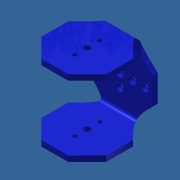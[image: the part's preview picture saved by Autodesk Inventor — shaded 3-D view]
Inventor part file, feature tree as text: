
AUTODESK INVENTOR PART (.ipt)
format: ipt  version: 2014 (Build 180170000, 170)  size: 280,576 bytes
history: native  units: in
note: dims shown in document units (in); Inventor stores cm internally (conversion verified against a paired STEP export)
features: extrude x7, sketch x7, plane x2, fillet x2, mirror x2, projected_geometry x2
ambient origin geometry x8: Origin, YZ Plane, XZ Plane, XY Plane, X Axis, Y Axis, Z Axis, Center Point
bodies: Solid1 (feature_tree)
feature tree (22):
  extrude  "Extrusion1"  TaperAngle=0.0deg  [1 undecoded]
  extrude  "Extrusion2"  Depth=0.1772in
  plane  "Work Plane1"
  extrude  "Extrusion3"  Depth=0.1772in
  fillet  "Fillet1"  [1 undecoded]
  plane  "Work Plane2"
  mirror  "Mirror1"
  fillet  "Fillet2"  Radius=0.1181in
  extrude  "Extrusion4"  Depth=0.5906in
  extrude  "Extrusion5"  Depth=0.1772in
  extrude  "Extrusion6"  Depth=0.2559in
  extrude  "Extrusion7"  Depth=0.3937in
  mirror  "Mirror2"
  sketch  "Sketch1"  dims[d0=2.0472in d3=0.0in]
  sketch  "Sketch2"  dims[d4=2.0472in d5=0.1772in]
  sketch  "Sketch3"  dims[d6=0.0in d7=0.1772in d8=0.0in d9=0.1181in]
  sketch  "Sketch4"  dims[d10=-1.0236in d11=0.5906in]
  sketch  "Sketch5"  dims[d12=0.1969in d15=0.1772in]
  sketch  "Sketch6"  dims[d16=0.0in d17=0.2559in]
  projected_geometry  "Projected Loop1"
  sketch  "Sketch7"  dims[d18=0.2559in d19=0.3937in d20=0.2559in d21=0.3937in d22=0.2559in d23=0.2559in d24=0.3937in d25=0.3937in d26=0.1181in d27=0.0in d28=0.2087in d29=0.2087in d30=0.2087in d31=0.2087in d32=0.2087in d33=0.0197in d34=0.2749in d35=0.1181in d36=0.3937in d37=0.1181in d38=0.3937in d39=0.0in d40=0.0in d41=0.2559in d42=0.2559in d43=0.3937in d44=0.2087in d45=0.2559in d46=0.2559in d47=0.3937in d48=0.2087in]
  projected_geometry  "Projected Loop2"
note: 2 required parameter values undecoded (feature->parameter linkage not recoverable at this tier; creation-order binding heuristic only, values carry confidence <= 0.55)
